# Revit family: Lighting_Outside_L&L_Luce&Light_Flori_1.2
name_source: partatom
category: Lighting Fixtures
units: mm (PartAtom-declared; Revit-internal decimal feet)

## family parameters
Cut with Voids When Loaded = No
Host = Face
Light Source = No
Part Type = Normal
Room Calculation Point = No
Round Connector Dimension = Use Diameter
Shared = No

## types (5) — shared parameters
Apparent Load = 7 VA
BIMobject category = Outside
BIMobject category code = lighting-outside
BIMobject main category = Lighting
BIMobject main category code = lighting
Brand url = https://www.lucelight.it
Date of publishing = 4/20/2017
Default Elevation = 1219 mm
Design country = Italy
Edition number = 1
Geometry Material = Luce&Light_Aluminum
Glass Material = Luce&Light_Glass
IFC Classification = Light Fixture
Installation instructions = https://www.lucelight.it
Luce-Light_Accessories = Honeycomb louvre, standard snoot, asymmetrical snoot, painted black light barn doors, stakes for installation in the ground, stake for wall-mounted installation
Luce-Light_Applications = Outdoor
Luce-Light_Body_material = Body in aluminium
Luce-Light_Classification = CE
Luce-Light_Color_Rendering_Index_CRI = 80
Luce-Light_Finishes_material = anthracite, grey, white, cor-ten
Luce-Light_IK = 07
Luce-Light_IP = 66
Luce-Light_LED_colour = white: 2700K, 3000K, 4000K, RGBW
Luce-Light_LED_light_sources = 1 power LED High Intensity, 3-step MacAdam, 50 000h L90 B10 (Ta 25°C), 1 RGBW LED group, 50000h L85 B10 (Ta 25°C)
Luce-Light_Mounting = surface mounted (ceiling, wall, ground, spike, fastener strap)
Luce-Light_Note = version with 24Vdc power supply available on request
Luce-Light_Optical_assembly = 9°, 15°, 31°, 36°, 10°x45°, 45°x10°, RGBW: 24°, 33°, 60°, 32°x61°, 61°x32°
Luce-Light_Power = 7W, RGBW: 13W
Luce-Light_Power_Class = A / A+ / A++
Luce-Light_Rated_power_input = 230Vac, RGBW: 24Vdc
Luce-Light_Screen_material = serigraphed, tempered, transparent extra-clear glass
Luce-Light_Total_flow_rate = 366 lm (3000K, 31°, CRI 80), 296 lm (3000K, 31°, CRI 90), RGBW: 304 lm, R: 52 lm G: 95 lm B: 31 lm W: 126 lm (4000K, 33°)
Manufacturer = L&L Luce&Light
Manufacturer country = Italy
Manufacturer name = L&L Luce&Light
Masterformat 2014 Code = 26 50 00
Masterformat 2014 Description = Lighting
Model = Flori 1.2
NBS Reference Code = 70-80
NBS Reference Description = Lighting Systems
Nominal height = 147 mm
Nominal width = 154 mm
OmniClass Code = 23-35 47 11
OmniClass Description = Lighting Fixtures
Product Guid = af3463ed-7d1b-436f-a385-b5336389013b
Product Material = Luce&Light_Aluminum
Product SKU = Flori
Product data url = https://bimobject.com
Product family = Outdoor
Product group = Projectors
Product url = https://www.lucelight.it
QR code = http://bimobject.com
Technical description = https://www.lucelight.it
UNSPSC Code = 3911
URL = https://www.lucelight.it
Uniclass 1.4 Code = L762214
Uniclass 1.4 Description = Light beam systems
Uniclass 2.0 Code = SS-70-80
Uniclass 2.0 Description = Lighting Systems
Uniclass 2015 Code = EF_70_80
Uniclass 2015 Name = Lighting
Uniformat II Code = D5020
Uniformat II Description = Lighting & Branch Wiring
Voltage = 230 V
Wattage Comments = 13 W
Weight Net (Kg) = 0.8

## per-type parameters (varying)
| type | Light Source |
| FLORI 1.2 L 60 RGBW 13W 24Vdc | Light_Source_face_based : FLORI 1.2 L 60 RGBW 13W 24Vdc |
| FLORI 1.2 M 33 RGBW 13W 24Vdc | Light_Source_face_based : FLORI 1.2 M 33 RGBW 13W 24Vdc |
| FLORI 1.2 S 24° RGBW 13W 24Vdc | Light_Source_face_based : FLORI 1.2 S 24° RGBW 13W 24Vdc |
| FLORI 1.2 W 32x61 RGBW 13W 24Vdc | Light_Source_face_based : FLORI 1.2 W 32x61 RGBW 13W 24Vdc |
| FLORI 1.2 X 61x32 RGBW 13W 24Vdc | Light_Source_face_based : FLORI 1.2 W 32x61 RGBW 13W 24Vdc |

## geometry (parser evidence)
native form markers: Blend x4, Sweep x9
no freeform markers — native parametric forms only
